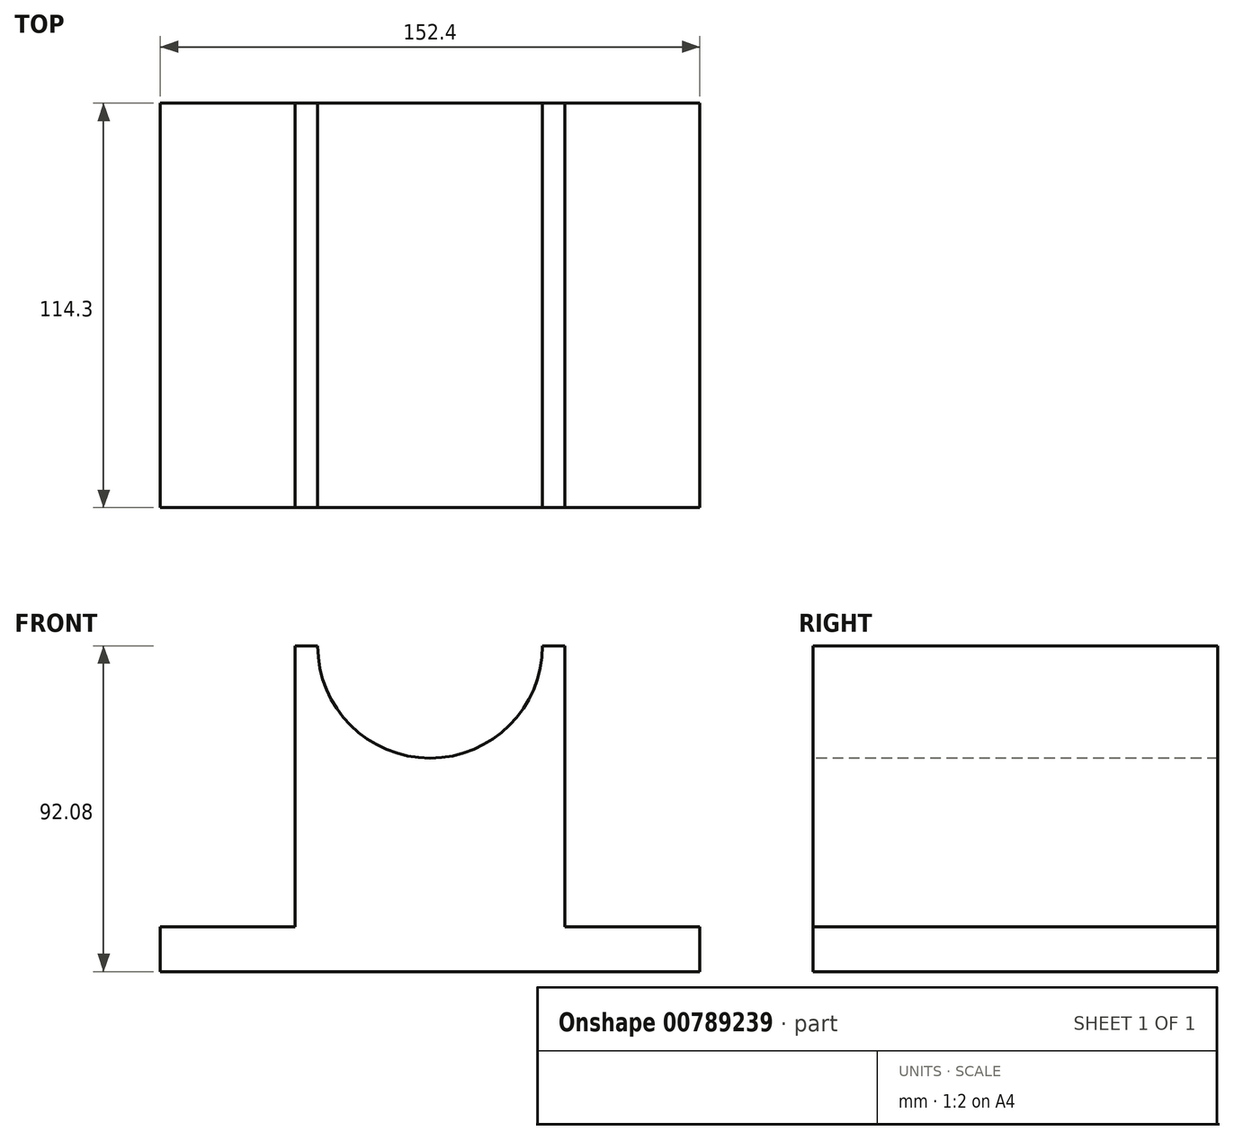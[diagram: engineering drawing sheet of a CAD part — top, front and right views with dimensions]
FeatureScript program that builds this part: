
annotation { "Feature Type Name" : "Feature", "Feature Type Description" : "" }
export const myFeature = defineFeature(function(context is Context, id is Id, definition is map)
    precondition{}
    {
        {
            var Q0;
            Q0=qCreatedBy(makeId("Front.planeOp"),FACE);
            var sketch = newSketch(context, id + "F0", { "sketchPlane" : qUnion([Q0])});
            skLineSegment(sketch, "E0", {"start": v(0, 0) * mm, "end": v(152.4, 0) * mm});
            skLineSegment(sketch, "E1", {"start": v(0, 0) * mm, "end": v(0, 12.7) * mm});
            skLineSegment(sketch, "E2", {"start": v(152.4, 0) * mm, "end": v(152.4, 12.7) * mm});
            skLineSegment(sketch, "E3", {"start": v(0, 12.7) * mm, "end": v(38.1, 12.7) * mm});
            skLineSegment(sketch, "E4", {"start": v(152.4, 12.7) * mm, "end": v(114.3, 12.7) * mm});
            skLineSegment(sketch, "E5", {"start": v(38.1, 12.7) * mm, "end": v(38.1, 92.07) * mm});
            skLineSegment(sketch, "E6", {"start": v(114.3, 12.7) * mm, "end": v(114.3, 92.08) * mm});
            skLineSegment(sketch, "E7", {"start": v(38.1, 92.07) * mm, "end": v(114.3, 92.07) * mm});
            skSolve(sketch);
        }
        {
            var Q0;
            Q0 = qSketchRegion(id + "F0", true);
            extrude(context, id + "F1", {"entities" : qUnion([Q0]), "depth" : 114.3 * mm, "offsetDistance" : 25.4 * mm});
        }
        {
            var Q0;
            Q0=makeQuery(id+"F1.opExtrude","CAP_FACE",FACE,{"disambiguationData":[OSD([sQuery(id+"F0.wireOp",EDGE,"E0"),sQuery(id+"F0.wireOp",EDGE,"E1"),sQuery(id+"F0.wireOp",EDGE,"E2"),sQuery(id+"F0.wireOp",EDGE,"E3"),sQuery(id+"F0.wireOp",EDGE,"E4"),sQuery(id+"F0.wireOp",EDGE,"E5"),sQuery(id+"F0.wireOp",EDGE,"E6"),sQuery(id+"F0.wireOp",EDGE,"E7")])],"isStart":false});
            var sketch = newSketch(context, id + "F2", { "sketchPlane" : qUnion([Q0])});
            skLineSegment(sketch, "E8", {"start": v(38.1, 92.07) * mm, "end": v(44.45, 92.07) * mm, "construction": true});
            skLineSegment(sketch, "E9", {"start": v(114.3, 92.07) * mm, "end": v(107.95, 92.07) * mm, "construction": true});
            skArc(sketch, "E10", {"start": v(44.45, 92.07) * mm, "mid": v(76.2, 60.32) * mm, "end": v(107.95, 92.07) * mm});
            skSolve(sketch);
        }
        {
            var Q0;
            {var subQ0=sQuery(id+"F2.wireOp",EDGE,"E10");Q0=makeQuery(id+"F2.imprint","IMPRINT",FACE,{"disambiguationData":[TD([[makeQuery(id+"F2.imprint","IMPRINT",EDGE,{"derivedFrom":subQ0}),1.0]])]});}
            extrude(context, id + "F3", {"entities" : qUnion([Q0]), "operationType" : NewBodyOperationType.REMOVE, "endBound" : BoundingType.THROUGH_ALL, "oppositeDirection" : true, "depth" : 25.4 * mm, "offsetDistance" : 25.4 * mm});
        }
    });
